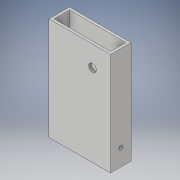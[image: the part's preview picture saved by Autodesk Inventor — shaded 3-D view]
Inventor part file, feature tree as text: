
AUTODESK INVENTOR PART (.ipt)
format: ipt  version: 2019 (Build 230136000, 136)  size: 132,608 bytes
history: native  units: in
note: dims shown in document units (in); Inventor stores cm internally (conversion verified against a paired STEP export)
features: sketch x6, extrude x4, hole x4
ambient origin geometry x8: Origin, YZ Plane, XZ Plane, XY Plane, X Axis, Y Axis, Z Axis, Center Point
bodies: Solid1 (feature_tree)
feature tree (14):
  extrude  "Extrusion1"  Depth=5.0in
  extrude  "Extrusion2"  Depth=1.0in
  extrude  "Extrusion3"  Depth=30.0in TaperAngle=0.0deg
  extrude  "Extrusion4"  Depth=0.125in TaperAngle=0.0deg
  hole  "Hole3"  [1 undecoded]
  hole  "Hole5"  [1 undecoded]
  sketch  "Sketch1"  dims[d0=3.0in d1=5.0in]
  sketch  "Sketch2"  dims[d2=1.0in d3=0.0in d4=0.813in]
  sketch  "Sketch4"  dims[d5=0.2031in d6=30.0in d7=0.0in]
  sketch  "Sketch5"  dims[d15=0.125in d16=20.0in d17=0.0in]
  sketch  "Sketch6"  dims[d18=0.5in d19=0.2031in]
  hole  "Hole2"  [1 undecoded]
  sketch  "Sketch7"  dims[d20=2.0in d21=0.0in d22=0.375in d23=0.75in d24=0.375in d25=0.25in d26=0.5635in d27=1.0in d28=0.0in d29=0.375in d30=0.75in d31=0.375in d32=0.25in d33=0.5635in d34=1.0in d35=0.0in]
  hole  "Hole4"  [1 undecoded]
note: 4 required parameter values undecoded (feature->parameter linkage not recoverable at this tier; creation-order binding heuristic only, values carry confidence <= 0.55)
